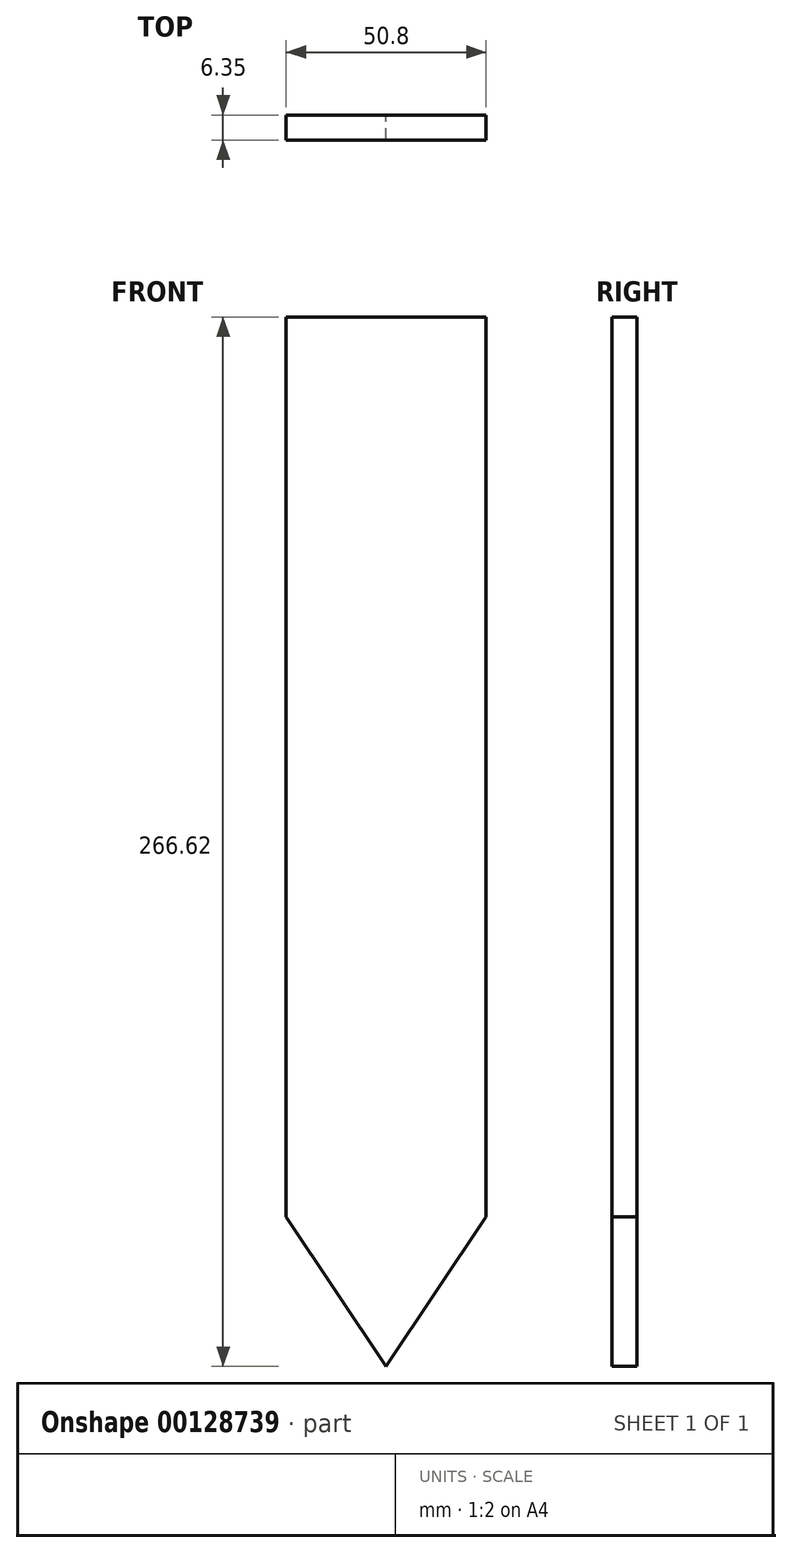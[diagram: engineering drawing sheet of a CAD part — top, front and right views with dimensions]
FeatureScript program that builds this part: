
annotation { "Feature Type Name" : "Feature", "Feature Type Description" : "" }
export const myFeature = defineFeature(function(context is Context, id is Id, definition is map)
    precondition{}
    {
        {
            var Q0;
            Q0=qCreatedBy(makeId("Front.planeOp"),FACE);
            var sketch = newSketch(context, id + "F0", { "sketchPlane" : qUnion([Q0])});
            skLineSegment(sketch, "E0.bottom", {"start": v(25.4, -114.3) * mm, "end": v(-25.4, -114.3) * mm});
            skLineSegment(sketch, "E0.top", {"start": v(25.4, 114.3) * mm, "end": v(-25.4, 114.3) * mm});
            skLineSegment(sketch, "E0.left", {"start": v(25.4, -114.3) * mm, "end": v(25.4, 114.3) * mm});
            skLineSegment(sketch, "E0.right", {"start": v(-25.4, -114.3) * mm, "end": v(-25.4, 114.3) * mm});
            skPoint(sketch, "E0.middle", {"position": v(0, 0) * mm});
            skLineSegment(sketch, "E1", {"start": v(-25.4, -114.3) * mm, "end": v(0, -152.32) * mm});
            skLineSegment(sketch, "E2", {"start": v(25.4, -114.3) * mm, "end": v(0, -152.32) * mm});
            skSolve(sketch);
        }
        {
            var Q0;
            Q0 = qSketchRegion(id + "F0", true);
            extrude(context, id + "F1", {"entities" : qUnion([Q0]), "depth" : 6.35 * mm});
        }
    });
